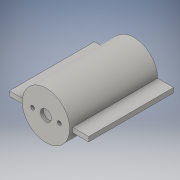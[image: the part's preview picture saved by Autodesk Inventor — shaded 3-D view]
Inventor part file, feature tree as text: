
AUTODESK INVENTOR PART (.ipt)
format: ipt  version: 2016 SP1 (Build 200210100, 210)  size: 136,192 bytes
history: native  units: in
note: dims shown in document units (in); Inventor stores cm internally (conversion verified against a paired STEP export)
features: extrude x3, sketch x3
ambient origin geometry x8: Origin, YZ Plane, XZ Plane, XY Plane, X Axis, Y Axis, Z Axis, Center Point
bodies: Body1 (feature_tree)
feature tree (6):
  extrude  "Extrusion2"  Depth=0.117in
  extrude  "Extrusion3"  Depth=1.984in
  extrude  "Extrusion4"  Depth=0.075in
  sketch  "Sketch1"  dims[d0=0.984in d4=0.117in]
  sketch  "Sketch2"  dims[d5=0.117in d6=1.984in]
  sketch  "Sketch3"  dims[d9=0.5in d12=0.984in d13=0.592in d14=0.592in d15=0.4117in d16=0.4117in d17=0.4in d18=2.125in d19=0.0in d20=0.28in d21=1.184in d22=0.075in d23=0.0in d25=0.0984in d26=0.3345in d27=0.0984in d28=0.3345in d29=10.0in d30=0.0in]
